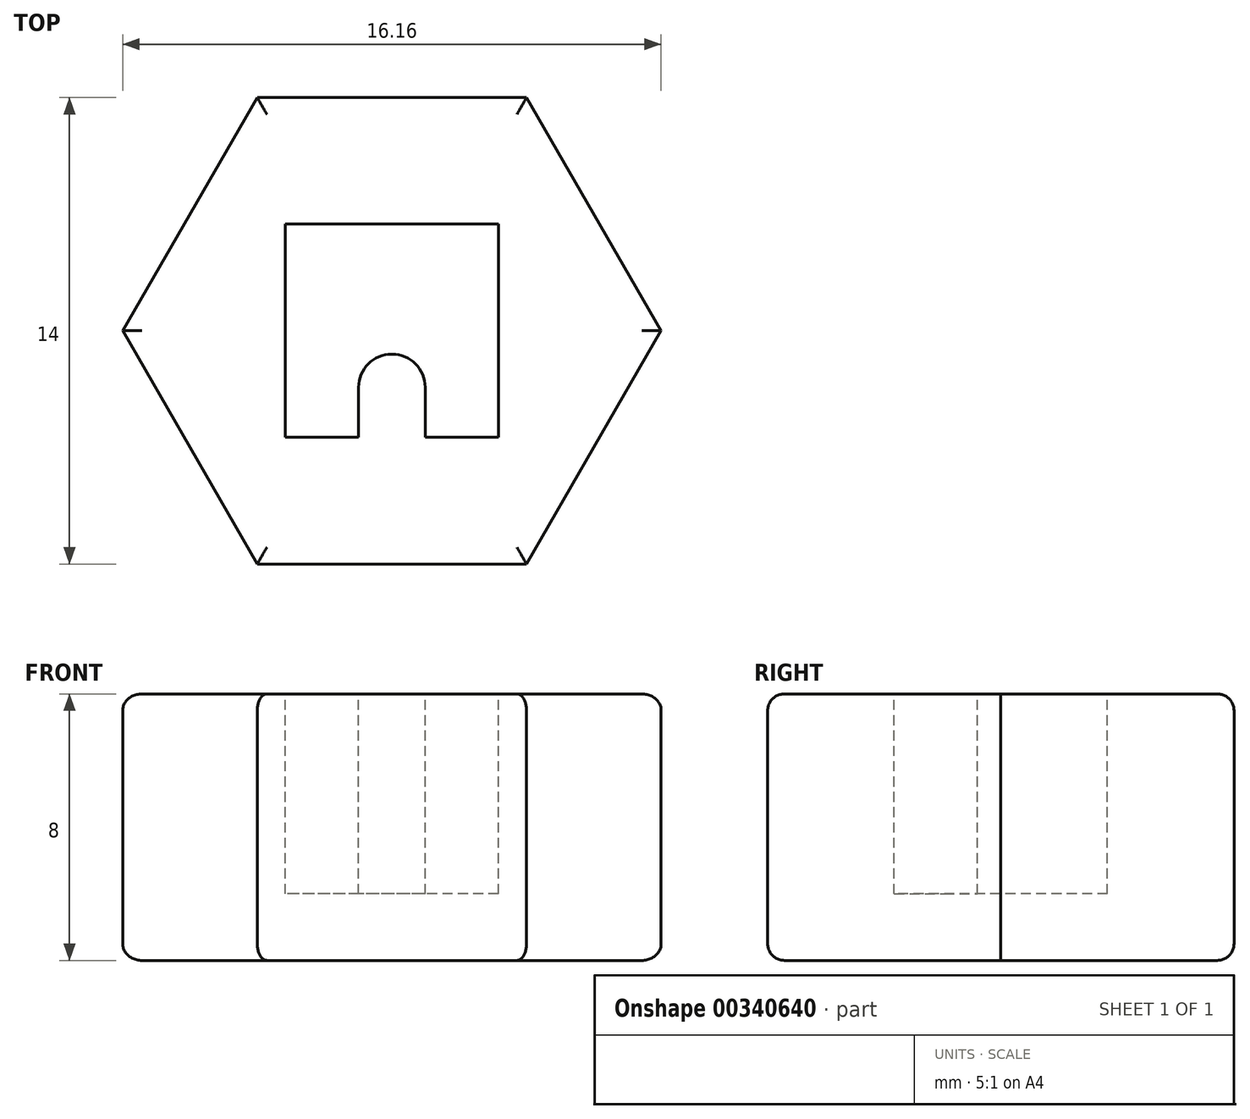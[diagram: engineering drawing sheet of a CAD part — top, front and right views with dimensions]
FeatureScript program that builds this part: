
annotation { "Feature Type Name" : "Feature", "Feature Type Description" : "" }
export const myFeature = defineFeature(function(context is Context, id is Id, definition is map)
    precondition{}
    {
        {
            var Q0;
            Q0=qCreatedBy(makeId("Top.planeOp"),FACE);
            var sketch = newSketch(context, id + "F0", { "sketchPlane" : qUnion([Q0])});
            skCircle(sketch, "E0.cCircle", {"center": v(0, 0) * mm, "radius": 7 * mm, "construction": true});
            skLineSegment(sketch, "E0.0", {"start": v(4.04, 7) * mm, "end": v(8.08, 0) * mm});
            skLineSegment(sketch, "E0.1", {"start": v(8.08, 0) * mm, "end": v(4.04, -7) * mm});
            skLineSegment(sketch, "E0.2", {"start": v(4.04, -7) * mm, "end": v(-4.04, -7) * mm});
            skLineSegment(sketch, "E0.3", {"start": v(-4.04, -7) * mm, "end": v(-8.08, 0) * mm});
            skLineSegment(sketch, "E0.4", {"start": v(-8.08, 0) * mm, "end": v(-4.04, 7) * mm});
            skLineSegment(sketch, "E0.5", {"start": v(-4.04, 7) * mm, "end": v(4.04, 7) * mm});
            skPoint(sketch, "E0.0.midPoint", {"position": v(6.06, 3.5) * mm});
            skSolve(sketch);
        }
        {
            var Q0;
            Q0=makeQuery(id+"F0.imprint","IMPRINT",FACE,{"disambiguationData":[TD([[makeQuery(id+"F0.imprint","IMPRINT",EDGE,{"derivedFrom":sQuery(id+"F0.wireOp",EDGE,"E0.0")}),-1.0]])]});
            extrude(context, id + "F1", {"entities" : qUnion([Q0]), "depth" : 8 * mm});
        }
        {
            var Q0;
            Q0=makeQuery(id+"F1.opExtrude","CAP_FACE",FACE,{"disambiguationData":[OSD([sQuery(id+"F0.wireOp",EDGE,"E0.0"),sQuery(id+"F0.wireOp",EDGE,"E0.1"),sQuery(id+"F0.wireOp",EDGE,"E0.2"),sQuery(id+"F0.wireOp",EDGE,"E0.3"),sQuery(id+"F0.wireOp",EDGE,"E0.4"),sQuery(id+"F0.wireOp",EDGE,"E0.5")])],"isStart":false});
            var sketch = newSketch(context, id + "F2", { "sketchPlane" : qUnion([Q0])});
            skLineSegment(sketch, "E1.bottom", {"start": v(3.2, 3.2) * mm, "end": v(-3.2, 3.2) * mm});
            skLineSegment(sketch, "E1.top", {"start": v(3.2, -3.2) * mm, "end": v(1, -3.2) * mm});
            skLineSegment(sketch, "E1.left", {"start": v(3.2, 3.2) * mm, "end": v(3.2, -3.2) * mm});
            skLineSegment(sketch, "E1.right", {"start": v(-3.2, 3.2) * mm, "end": v(-3.2, -3.2) * mm});
            skPoint(sketch, "E1.middle", {"position": v(0, 0) * mm});
            skLineSegment(sketch, "E2", {"start": v(-1, -3.2) * mm, "end": v(-1, -1.7) * mm});
            skLineSegment(sketch, "E3", {"start": v(-1, -1.7) * mm, "end": v(1, -1.7) * mm, "construction": true});
            skLineSegment(sketch, "E4", {"start": v(1, -1.7) * mm, "end": v(1, -3.2) * mm});
            skLineSegment(sketch, "E5", {"start": v(0, -1.7) * mm, "end": v(0, 0) * mm, "construction": true});
            skLineSegment(sketch, "E6", {"start": v(-1, -3.2) * mm, "end": v(-3.2, -3.2) * mm});
            skLineSegment(sketch, "E7", {"start": v(1, -3.2) * mm, "end": v(-1, -3.2) * mm, "construction": true});
            skArc(sketch, "E8", {"start": v(1, -1.7) * mm, "mid": v(0, -0.7) * mm, "end": v(-1, -1.7) * mm});
            skSolve(sketch);
        }
        {
            var Q0;
            Q0 = qSketchRegion(id + "F2", true);
            extrude(context, id + "F3", {"entities" : qUnion([Q0]), "operationType" : NewBodyOperationType.REMOVE, "oppositeDirection" : true, "depth" : 6 * mm});
        }
        {
            var Q0;
            Q0=makeQuery(id+"F1.opExtrude","CAP_EDGE",EDGE,{"disambiguationData":[OSD([sQuery(id+"F0.wireOp",EDGE,"E0.3")])],"isStart":true});
            var Q1;
            Q1=makeQuery(id+"F1.opExtrude","CAP_EDGE",EDGE,{"disambiguationData":[OSD([sQuery(id+"F0.wireOp",EDGE,"E0.2")])],"isStart":true});
            var Q2;
            Q2=makeQuery(id+"F1.opExtrude","CAP_EDGE",EDGE,{"disambiguationData":[OSD([sQuery(id+"F0.wireOp",EDGE,"E0.1")])],"isStart":true});
            var Q3;
            Q3=makeQuery(id+"F1.opExtrude","CAP_EDGE",EDGE,{"disambiguationData":[OSD([sQuery(id+"F0.wireOp",EDGE,"E0.0")])],"isStart":true});
            var Q4;
            Q4=makeQuery(id+"F1.opExtrude","CAP_EDGE",EDGE,{"disambiguationData":[OSD([sQuery(id+"F0.wireOp",EDGE,"E0.5")])],"isStart":true});
            var Q5;
            Q5=makeQuery(id+"F1.opExtrude","CAP_EDGE",EDGE,{"disambiguationData":[OSD([sQuery(id+"F0.wireOp",EDGE,"E0.4")])],"isStart":true});
            var Q6;
            Q6=makeQuery(id+"F1.opExtrude","CAP_EDGE",EDGE,{"disambiguationData":[OSD([sQuery(id+"F0.wireOp",EDGE,"E0.2")])],"isStart":false});
            var Q7;
            Q7=makeQuery(id+"F1.opExtrude","CAP_EDGE",EDGE,{"disambiguationData":[OSD([sQuery(id+"F0.wireOp",EDGE,"E0.1")])],"isStart":false});
            var Q8;
            Q8=makeQuery(id+"F1.opExtrude","CAP_EDGE",EDGE,{"disambiguationData":[OSD([sQuery(id+"F0.wireOp",EDGE,"E0.0")])],"isStart":false});
            var Q9;
            Q9=makeQuery(id+"F1.opExtrude","CAP_EDGE",EDGE,{"disambiguationData":[OSD([sQuery(id+"F0.wireOp",EDGE,"E0.5")])],"isStart":false});
            var Q10;
            Q10=makeQuery(id+"F1.opExtrude","CAP_EDGE",EDGE,{"disambiguationData":[OSD([sQuery(id+"F0.wireOp",EDGE,"E0.4")])],"isStart":false});
            var Q11;
            Q11=makeQuery(id+"F1.opExtrude","CAP_EDGE",EDGE,{"disambiguationData":[OSD([sQuery(id+"F0.wireOp",EDGE,"E0.3")])],"isStart":false});
            fillet(context, id + "F4", {"entities" : qUnion([Q0, Q1, Q2, Q3, Q4, Q5, Q6, Q7, Q8, Q9, Q10, Q11]), "radius" : 0.5 * mm, "tangentPropagation" : true, "allowEdgeOverflow" : false});
        }
    });
